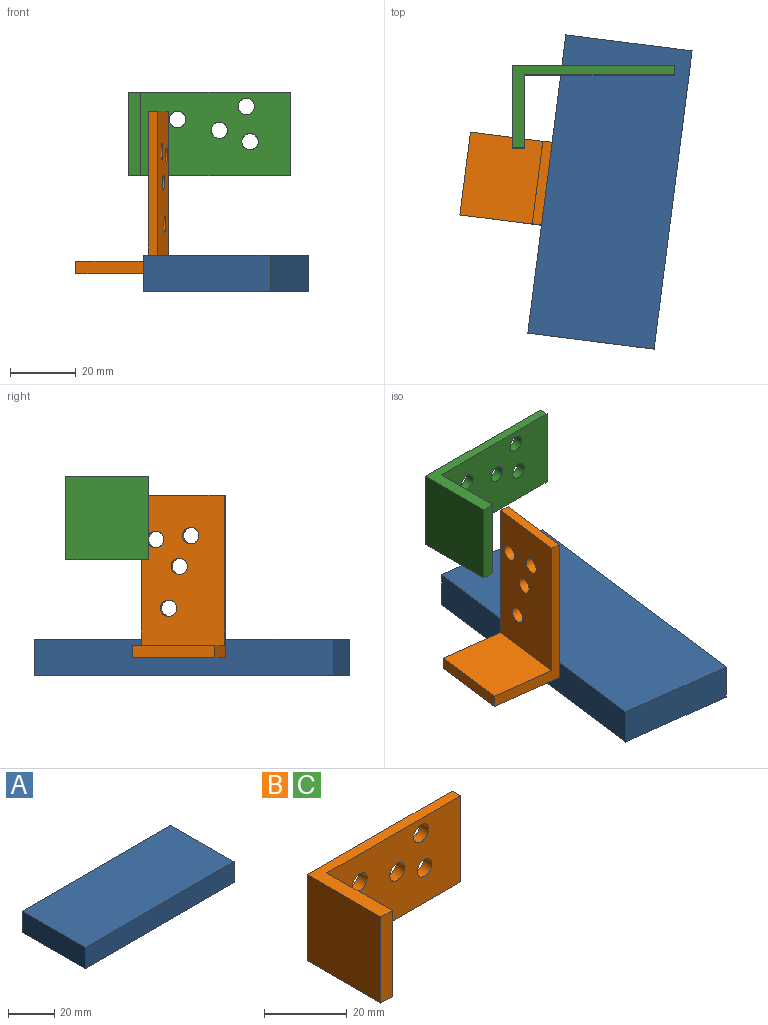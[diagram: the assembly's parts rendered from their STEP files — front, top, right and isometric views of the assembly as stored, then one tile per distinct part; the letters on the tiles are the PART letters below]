
ASSEMBLY  parts=3 mates=1
PART A: 6 faces, bbox 91.5x38.7x11.2 mm
  f0: plane 91.49x11.18mm, normal (0,1,0), area 1022.5mm2, adj f1,f3,f4,f5
  f1: plane 38.72x11.18mm, normal (-1,0,0), area 432.8mm2, adj f0,f2,f4,f5
  f2: plane 91.49x11.18mm, normal (0,-1,0), area 1022.5mm2, adj f1,f3,f4,f5
  f3: plane 38.72x11.18mm, normal (1,0,0), area 432.8mm2, adj f0,f2,f4,f5
  f4: plane 91.49x38.72mm, normal (0,0,1), area 3543mm2, adj f0,f1,f2,f3
  f5: plane 91.49x38.72mm, normal (0,0,-1), area 3543mm2, adj f0,f1,f2,f3
PART B: 12 faces, bbox 49.4x25.1x25.4 mm
  f0: plane 25.4x25.06mm, normal (-1,0,0), area 636.4mm2, adj f1,f5,f6,f7
  f1: plane 25.4x3.8mm, normal (0,-1,0), area 96.4mm2, adj f0,f2,f6,f7
  f2: plane 25.4x22.21mm, normal (1,0,0), area 564.1mm2, adj f1,f3,f6,f7
  f3: plane 45.56x25.4mm, normal (0,-1,0), area 1078.6mm2, adj f2,f4,f6,f7,f8,f9,f10,f11
  f4: plane 25.4x2.85mm, normal (1,0,0), area 72.3mm2, adj f3,f5,f6,f7
  f5: plane 49.35x25.4mm, normal (0,1,0), area 1175mm2, adj f0,f4,f6,f7,f8,f9,f10,f11
  f6: plane 49.35x25.06mm, normal (0,0,1), area 224.8mm2, adj f0,f1,f2,f3,f4,f5
  f7: plane 49.35x25.06mm, normal (0,0,-1), area 224.8mm2, adj f0,f1,f2,f3,f4,f5
  f8: cylinder r=2.5mm len=5mm, axis (0,-1,0), area 44.7mm2, adj f3,f5
  f9: cylinder r=2.5mm len=5mm, axis (0,-1,0), area 44.7mm2, adj f3,f5
  f10: cylinder r=2.5mm len=5mm, axis (0,-1,0), area 44.7mm2, adj f3,f5
  f11: cylinder r=2.5mm len=5mm, axis (0,-1,0), area 44.7mm2, adj f3,f5
PART C: same geometry as B
PLACE A rot(axis=(0.75,0.66,0),180deg) t=(-24.74,-25.02,5.22)mm
PLACE B rot(axis=(-0.6,-0.53,-0.6),124.3deg) t=(-55.33,-23.3,20.61)mm
PLACE C t=(-32.74,13.24,29.45)mm
MATE fastened A.f2 <-> B.f5  axis (0.99,-0.13,0) through (-43.18,-12.05,-0.37)mm
